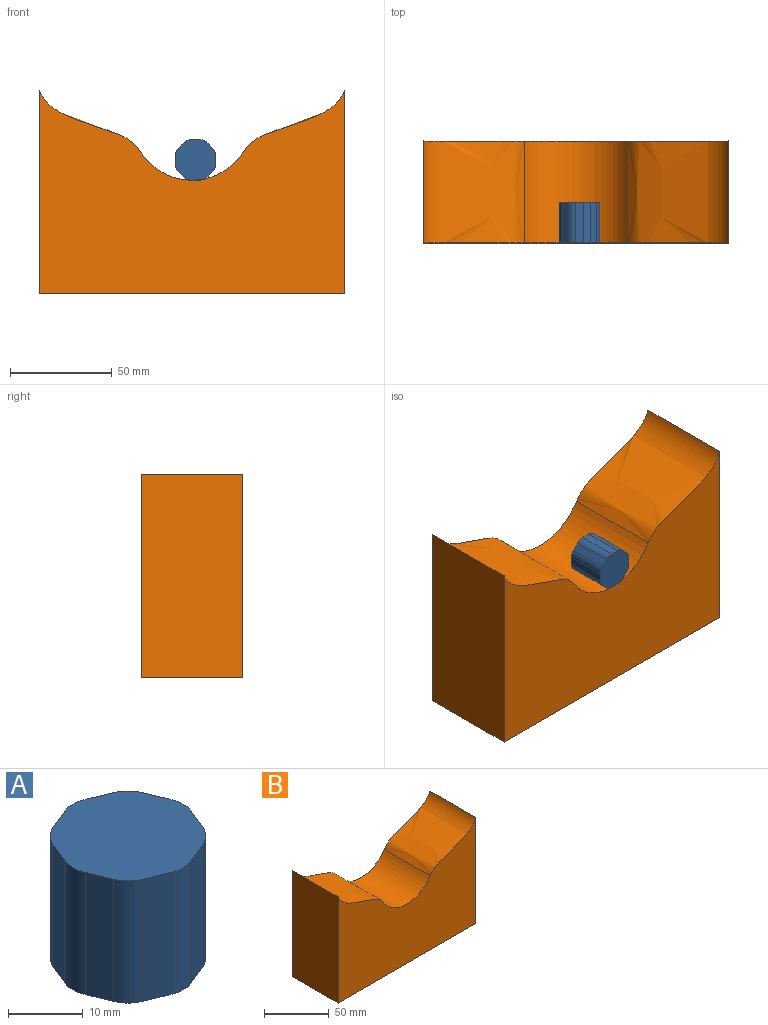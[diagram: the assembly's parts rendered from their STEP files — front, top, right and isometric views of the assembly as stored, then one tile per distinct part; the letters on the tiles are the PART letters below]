
ASSEMBLY  parts=2 mates=1
PART A: 18 faces, bbox 20.8x20.8x20 mm
  f0: plane 20x3.83mm, normal (-0.92,0.38,0), area 82.8mm2, adj f8,f9,f10,f17
  f1: plane 20x3.83mm, normal (-0.92,-0.38,0), area 82.8mm2, adj f8,f9,f10,f11
  f2: plane 20x3.83mm, normal (-0.38,-0.92,0), area 82.8mm2, adj f8,f9,f11,f12
  f3: plane 20x3.83mm, normal (0.38,-0.92,0), area 82.8mm2, adj f8,f9,f12,f13
  f4: plane 20x3.83mm, normal (0.92,-0.38,0), area 82.8mm2, adj f8,f9,f13,f14
  f5: plane 20x3.83mm, normal (0.92,0.38,0), area 82.8mm2, adj f8,f9,f14,f15
  f6: plane 20x3.83mm, normal (0.38,0.92,0), area 82.8mm2, adj f8,f9,f15,f16
  f7: plane 20x3.83mm, normal (-0.38,0.92,0), area 82.8mm2, adj f8,f9,f16,f17
  f8: plane 20.82x20.82mm, normal (0,0,1), area 327.1mm2, adj f0,f1,f2,f3,f4,f5,f6,f7
  f9: plane 20.82x20.82mm, normal (0,0,-1), area 327.1mm2, adj f0,f1,f2,f3,f4,f5,f6,f7
  f10: cylinder r=5mm len=20mm, axis (0,0,-1), area 78.5mm2, adj f0,f1,f8,f9
  f11: cylinder r=5mm len=20mm, axis (0,0,-1), area 78.5mm2, adj f1,f2,f8,f9
  f12: cylinder r=5mm len=20mm, axis (0,0,-1), area 78.5mm2, adj f2,f3,f8,f9
  f13: cylinder r=5mm len=20mm, axis (0,0,-1), area 78.5mm2, adj f3,f4,f8,f9
  f14: cylinder r=5mm len=20mm, axis (0,0,-1), area 78.5mm2, adj f4,f5,f8,f9
  f15: cylinder r=5mm len=20mm, axis (0,0,-1), area 78.5mm2, adj f5,f6,f8,f9
  f16: cylinder r=5mm len=20mm, axis (0,0,-1), area 78.5mm2, adj f6,f7,f8,f9
  f17: cylinder r=5mm len=20mm, axis (0,0,-1), area 78.5mm2, adj f0,f7,f8,f9
PART B: 8 faces, bbox 150x50x100 mm
  f0: plane 150x50mm, normal (0,0,-1), area 7500mm2, adj f1,f4,f5,f6
  f1: plane 100x50mm, normal (1,0,0), area 5000mm2, adj f0,f2,f5,f6
  f2: extruded ~50x49.64mm, area 2996.9mm2, adj f1,f5,f6,f7
  f3: extruded ~50x49.64mm, area 2996.9mm2, adj f4,f5,f6,f7
  f4: plane 100x50mm, normal (-1,0,0), area 5000mm2, adj f0,f3,f5,f6
  f5: plane 150x100mm, normal (0,-1,0), area 11346.9mm2, adj f0,f1,f2,f3,f4,f7
  f6: plane 150x100mm, normal (0,1,0), area 11346.9mm2, adj f0,f1,f2,f3,f4,f7
  f7: cylinder r=30mm len=50.72mm, axis (0,1,0), area 3021.9mm2, adj f2,f3,f5,f6
PLACE A rot(axis=(0.96,-0.19,0.19),92.2deg) t=(586.85,77.34,225.42)mm
PLACE B t=(585.08,107.34,209.62)mm fixed
MATE planar A.f8 <-> B.f5  axis (0,-1,0) through (586.85,57.34,225.42)mm
